# Revit family: Door-NanaWall-HSW60_Concept_E
name_source: partatom
category: Doors
units: mm (PartAtom-declared; Revit-internal decimal feet)

## family parameters
Always vertical = Yes
Classification Number = 23.30.10.17.11
Cut with Voids When Loaded = No
Host = Wall
Room Calculation Point = No
Shared = No

## types (4) — shared parameters
04 CSI = 08 41 13
95 CSI = 8411
Analytic Construction = <None>
Assembly Code = B2030110
Cost Info = https://www.nanawall.com
Description = Single Track Sliding System
Detail Component in Plan = Yes
Detail Component in Section = Yes
Engineering Details URL = https://www.nanawall.com
Glass Material = Glass - NanaWall - Generic
Glazing Options = https://www.nanawall.com
Glazing Thickness = 241/256"
Green Building-LEED = https://www.arcat.com
Height = 9' - 0"
Height Constraint = 9' - 0"
Installation and Service URL = https://www.nanawall.com
Jamb Height = 9' - 0 61/64"
Keynote = 08 41 00
Manufacturer = NanaWall Systems, Inc.
Manufacturer Fax = (415) 383-0312
Manufacturer Website = https://www.nanawall.com
Model = HSW60 - Concept E
NanaWall Configurator = http://www.nanawall.com
Opening Width = 9' - 7 107/256"
Performance URL = https://www.nanawall.com
Product Data = https://www.arcat.com
Product Page URL = https://www.nanawall.com
Rough Height = 9' - 0"
Rough Width = 9' - 10 7/64"
Sales Information = https://www.nanawall.com
Sash = Metal - NanaWall - Aluminum
Sills Available = Surface Mounted, Floor Sockets, Low Profile Saddle, Flush
Size Note = Adjust Height and Width as necessary to fit your project needs. Multiple Panel and opening configurations are available. See Product Page URL for more information.
Specification = https://www.arcat.com
Subcategory = Sliding Glass Wall
Thickness = 2 1/2"
URL = http://www.nanawall.com
Wall Closure = By host
Warranty URL = http://www.nanawall.com
Width = 10' - 0"
Width C = 10' - 0"
not DIP = No
zero-valued in all types: Cost

## per-type parameters (varying)
| type | Flush Sill | Low Profile Saddle Sill | No Sill - Floor Socket | Surface Mounted Sill |
| HSW60-Configuration_E Surface Mounted Sill | No | No | No | Yes |
| HSW60-Configuration_E Low Profile Saddle Sill | No | Yes | No | No |
| HSW60-Configuration_E Flush Sill | Yes | No | No | No |
| HSW60-Configuration_E No Sill - Floor Sockets | No | No | Yes | No |

## geometry (parser evidence)
native form markers: Blend x846, Sweep x37
no freeform markers — native parametric forms only
